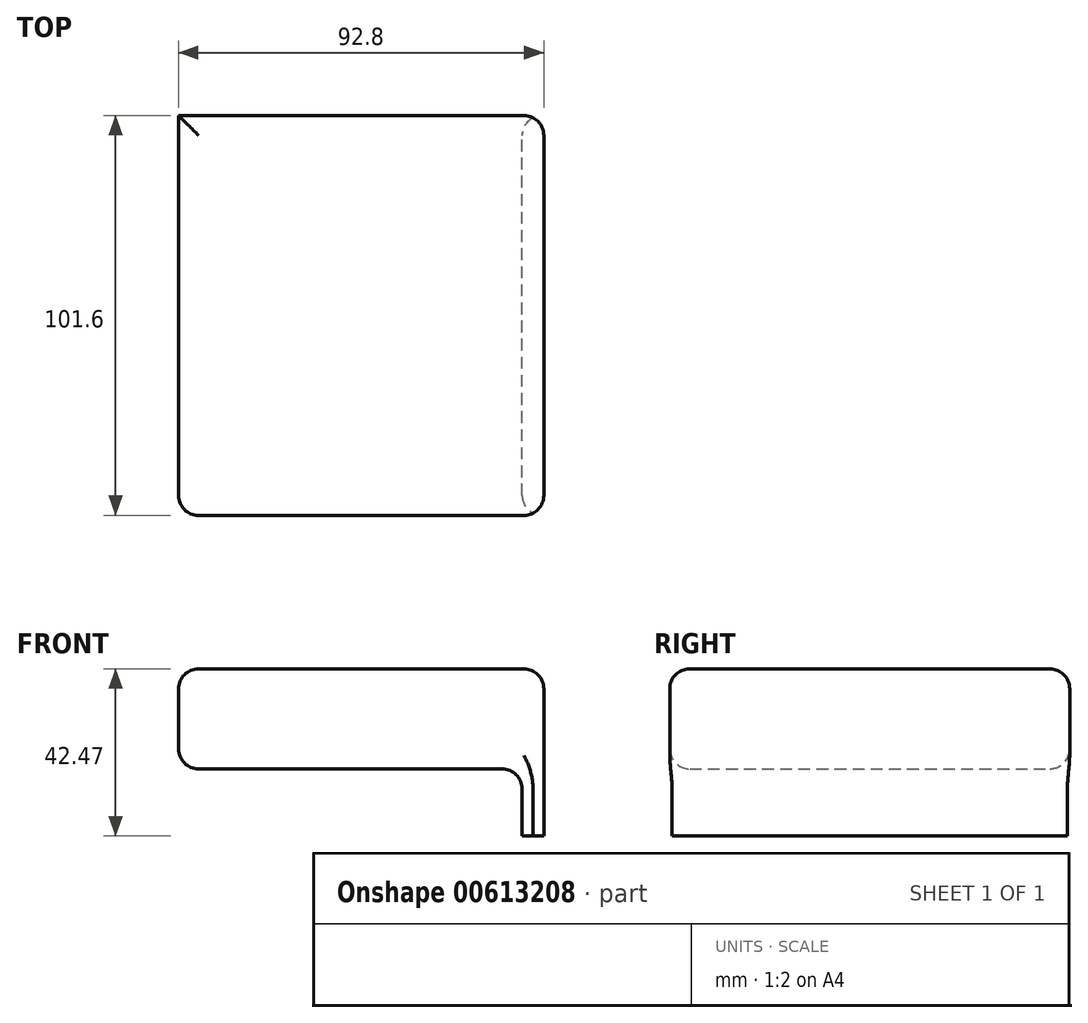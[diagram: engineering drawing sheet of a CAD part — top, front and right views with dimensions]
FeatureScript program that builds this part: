
annotation { "Feature Type Name" : "Feature", "Feature Type Description" : "" }
export const myFeature = defineFeature(function(context is Context, id is Id, definition is map)
    precondition{}
    {
        {
            var Q0;
            Q0=qCreatedBy(makeId("Front.planeOp"),FACE);
            var sketch = newSketch(context, id + "F0", { "sketchPlane" : qUnion([Q0])});
            skLineSegment(sketch, "E0", {"start": v(-128.5, 25.4) * mm, "end": v(-47.23, 25.4) * mm});
            skLineSegment(sketch, "E1", {"start": v(-41.23, 0) * mm, "end": v(-128.5, 0) * mm});
            skLineSegment(sketch, "E2", {"start": v(-128.5, 0) * mm, "end": v(-128.5, 25.4) * mm});
            skLineSegment(sketch, "E3", {"start": v(-47.23, 25.4) * mm, "end": v(-35.71, 25.4) * mm});
            skLineSegment(sketch, "E4", {"start": v(-35.71, 25.4) * mm, "end": v(-35.71, -17.07) * mm});
            skLineSegment(sketch, "E5", {"start": v(-35.71, -17.07) * mm, "end": v(-41.23, -17.07) * mm});
            skLineSegment(sketch, "E6", {"start": v(-41.23, 0) * mm, "end": v(-41.23, -17.07) * mm});
            skSolve(sketch);
        }
        {
            var Q0;
            Q0 = qSketchRegion(id + "F0", true);
            extrude(context, id + "F1", {"entities" : qUnion([Q0]), "depth" : 101.6 * mm, "offsetDistance" : 25.4 * mm});
        }
        {
            var Q0;
            Q0=makeQuery(id+"F1.opExtrude","SWEPT_EDGE",EDGE,{"disambiguationData":[OSD([sQuery(id+"F0.wireOp",EDGE,"E1"),sQuery(id+"F0.wireOp",EDGE,"E6")])]});
            var Q1;
            Q1=makeQuery(id+"F1.opExtrude","CAP_EDGE",EDGE,{"disambiguationData":[OSD([sQuery(id+"F0.wireOp",EDGE,"E6")])],"isStart":true});
            var Q2;
            Q2=makeQuery(id+"F1.opExtrude","SWEPT_FACE",FACE,{"disambiguationData":[OSD([sQuery(id+"F0.wireOp",EDGE,"E1")])]});
            var Q3;
            Q3=makeQuery(id+"F1.opExtrude","CAP_EDGE",EDGE,{"disambiguationData":[OSD([sQuery(id+"F0.wireOp",EDGE,"E4")])],"isStart":false});
            var Q4;
            Q4=makeQuery(id+"F1.opExtrude","CAP_EDGE",EDGE,{"disambiguationData":[OSD([sQuery(id+"F0.wireOp",EDGE,"E6")])],"isStart":false});
            var Q5;
            Q5=makeQuery(id+"F1.opExtrude","SWEPT_EDGE",EDGE,{"disambiguationData":[OSD([sQuery(id+"F0.wireOp",EDGE,"E3"),sQuery(id+"F0.wireOp",EDGE,"E4")])]});
            var Q6;
            Q6=makeQuery(id+"F1.opExtrude","CAP_EDGE",EDGE,{"disambiguationData":[OSD([sQuery(id+"F0.wireOp",EDGE,"E0"),sQuery(id+"F0.wireOp",EDGE,"E3")])],"isStart":true});
            var Q7;
            Q7=makeQuery(id+"F1.opExtrude","CAP_EDGE",EDGE,{"disambiguationData":[OSD([sQuery(id+"F0.wireOp",EDGE,"E4")])],"isStart":true});
            var Q8;
            Q8=makeQuery(id+"F1.opExtrude","SWEPT_EDGE",EDGE,{"disambiguationData":[OSD([sQuery(id+"F0.wireOp",EDGE,"E0"),sQuery(id+"F0.wireOp",EDGE,"E2")])]});
            fillet(context, id + "F2", {"entities" : qUnion([Q0, Q1, Q2, Q3, Q4, Q5, Q6, Q7, Q8]), "radius" : 5.08 * mm, "tangentPropagation" : true, "allowEdgeOverflow" : false});
        }
        {
            var Q0;
            Q0=makeQuery(id+"F1.opExtrude","CAP_EDGE",EDGE,{"disambiguationData":[OSD([sQuery(id+"F0.wireOp",EDGE,"E0"),sQuery(id+"F0.wireOp",EDGE,"E3")])],"isStart":false});
            fillet(context, id + "F3", {"entities" : qUnion([Q0]), "radius" : 5.08 * mm, "tangentPropagation" : true, "allowEdgeOverflow" : false});
        }
    });
